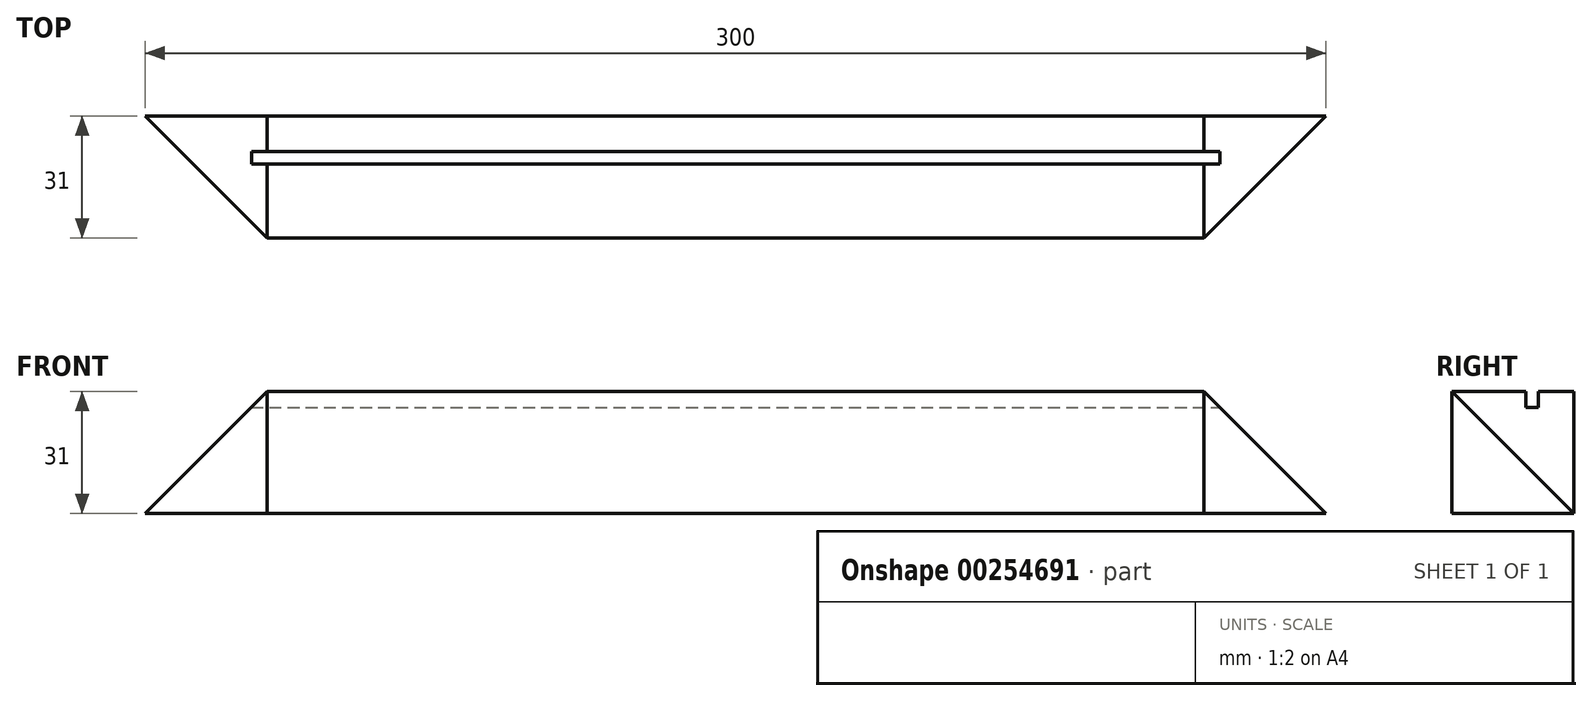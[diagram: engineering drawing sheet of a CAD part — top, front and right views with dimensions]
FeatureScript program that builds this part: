
annotation { "Feature Type Name" : "Feature", "Feature Type Description" : "" }
export const myFeature = defineFeature(function(context is Context, id is Id, definition is map)
    precondition{}
    {
        {
            var Q0;
            Q0=qCreatedBy(makeId("Top.planeOp"),FACE);
            var sketch = newSketch(context, id + "F0", { "sketchPlane" : qUnion([Q0])});
            skLineSegment(sketch, "E0.bottom", {"start": v(31, 0) * mm, "end": v(269, 0) * mm});
            skLineSegment(sketch, "E0.top", {"start": v(0, 31) * mm, "end": v(300, 31) * mm});
            skLineSegment(sketch, "E1", {"start": v(0, 31) * mm, "end": v(31, 0) * mm});
            skLineSegment(sketch, "E2", {"start": v(150, 31) * mm, "end": v(150, 0) * mm, "construction": true});
            skLineSegment(sketch, "E3.MirrorCS", {"start": v(300, 31) * mm, "end": v(269, 0) * mm});
            skSolve(sketch);
        }
        {
            var Q0;
            Q0=qSketchRegion(id+"F0",true);
            extrude(context, id + "F1", {"entities" : qUnion([Q0]), "depth" : 31 * mm});
        }
        {
            var Q0;
            Q0=makeQuery(id+"F1.opExtrude","SWEPT_FACE",FACE,{"disambiguationData":[OSD([sQuery(id+"F0.wireOp",EDGE,"E0.top")])]});
            var sketch = newSketch(context, id + "F2", { "sketchPlane" : qUnion([Q0])});
            skLineSegment(sketch, "E4", {"start": v(0, 0) * mm, "end": v(0, 31) * mm});
            skLineSegment(sketch, "E5", {"start": v(0, 31) * mm, "end": v(-31, 31) * mm});
            skLineSegment(sketch, "E6", {"start": v(-31, 31) * mm, "end": v(0, 0) * mm});
            skLineSegment(sketch, "E7", {"start": v(-150, 31) * mm, "end": v(-150, 0) * mm, "construction": true});
            skLineSegment(sketch, "E8.MirrorCS", {"start": v(-269, 31) * mm, "end": v(-300, 0) * mm});
            skLineSegment(sketch, "E9.MirrorCS", {"start": v(-300, 0) * mm, "end": v(-300, 31) * mm});
            skLineSegment(sketch, "E10.MirrorCS", {"start": v(-300, 31) * mm, "end": v(-269, 31) * mm});
            skSolve(sketch);
        }
        {
            var Q0;
            Q0=qSketchRegion(id+"F2",true);
            extrude(context, id + "F3", {"entities" : qUnion([Q0]), "operationType" : NewBodyOperationType.REMOVE, "endBound" : BoundingType.THROUGH_ALL, "oppositeDirection" : true, "depth" : 25 * mm});
        }
        {
            var Q0;
            Q0=makeQuery(id+"F1.opExtrude","CAP_FACE",FACE,{"disambiguationData":[OSD([sQuery(id+"F0.wireOp",EDGE,"E0.bottom"),sQuery(id+"F0.wireOp",EDGE,"E0.top"),sQuery(id+"F0.wireOp",EDGE,"E1"),sQuery(id+"F0.wireOp",EDGE,"E3.MirrorCS")])],"isStart":false});
            var sketch = newSketch(context, id + "F4", { "sketchPlane" : qUnion([Q0])});
            skPoint(sketch, "E11.oppositeSnap0", {"position": v(269, 15.5) * mm});
            skLineSegment(sketch, "E12.bottom", {"start": v(27, 22) * mm, "end": v(273, 22) * mm});
            skLineSegment(sketch, "E12.top", {"start": v(27, 18.8) * mm, "end": v(273, 18.8) * mm});
            skLineSegment(sketch, "E12.left", {"start": v(27, 22) * mm, "end": v(27, 18.8) * mm});
            skLineSegment(sketch, "E12.right", {"start": v(273, 22) * mm, "end": v(273, 18.8) * mm});
            skLineSegment(sketch, "E13", {"start": v(150, 22) * mm, "end": v(150, 18.8) * mm, "construction": true});
            skSolve(sketch);
        }
        {
            var Q0;
            Q0 = qSketchRegion(id + "F4", true);
            extrude(context, id + "F5", {"entities" : qUnion([Q0]), "operationType" : NewBodyOperationType.REMOVE, "oppositeDirection" : true, "depth" : 4 * mm});
        }
        {
            var Q0;
            Q0=sQuery(id+"F0.wireOp",VERTEX,"E1.start");
            var Q1;
            Q1=makeQuery(id+"F1.opExtrude","CAP_VERTEX",VERTEX,{"disambiguationData":[OSD([sQuery(id+"F0.wireOp",EDGE,"E0.bottom"),sQuery(id+"F0.wireOp",EDGE,"E1")])],"isStart":false});
            var Q2;
            Q2=makeQuery(id+"F1.opExtrude","CAP_VERTEX",VERTEX,{"disambiguationData":[OSD([sQuery(id+"F0.wireOp",EDGE,"E0.bottom"),sQuery(id+"F0.wireOp",EDGE,"E3.MirrorCS")])],"isStart":false});
            cPlane(context, id + "F6", {"entities" : qUnion([Q0, Q1, Q2]), "cplaneType" : CPlaneType.THREE_POINT, "offset" : 25 * mm, "oppositeDirection" : true, "width" : 150 * mm, "height" : 150 * mm});
        }
    });
